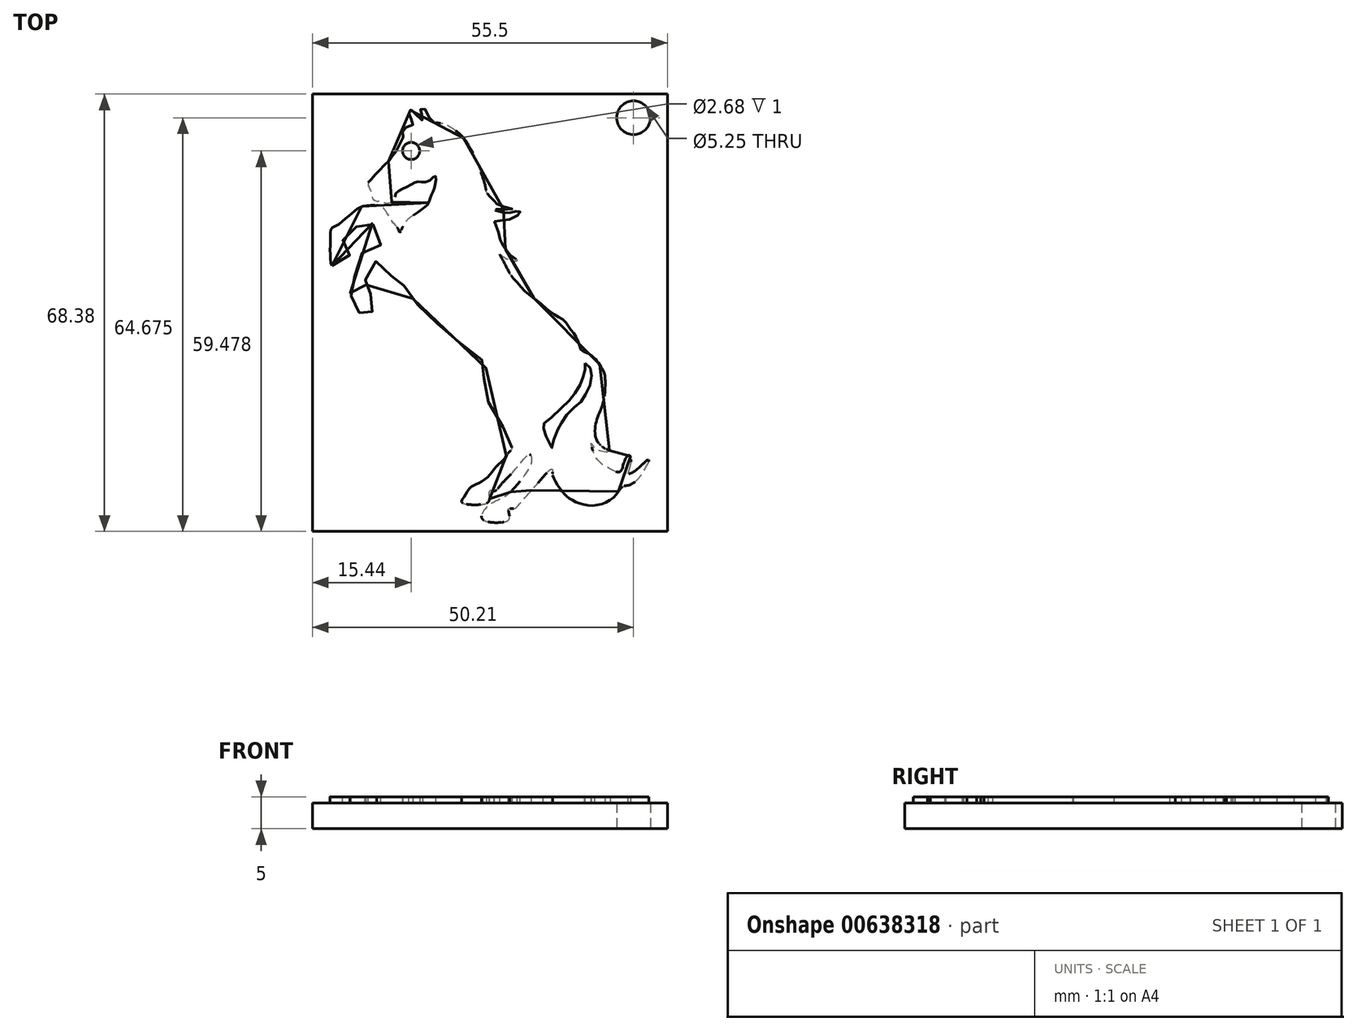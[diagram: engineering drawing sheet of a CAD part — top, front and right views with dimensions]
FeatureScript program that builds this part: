
annotation { "Feature Type Name" : "Feature", "Feature Type Description" : "" }
export const myFeature = defineFeature(function(context is Context, id is Id, definition is map)
    precondition{}
    {
        {
            var Q0;
            Q0=qCreatedBy(makeId("Top.planeOp"),FACE);
            var sketch = newSketch(context, id + "F0", { "sketchPlane" : qUnion([Q0])});
            skFitSpline(sketch, "E0", {"points": [v(-65.46, 22.42) * mm, v(-64.16, 22.86) * mm, v(-63.1, 23.72) * mm, v(-62.52, 24.42) * mm, v(-62.76, 25.41) * mm, v(-63.5, 26.06) * mm, v(-63.75, 26.7) * mm, v(-63.2, 27) * mm, v(-62.44, 27.85) * mm, v(-60.34, 29.37) * mm, v(-59.9, 29.52) * mm, v(-59.26, 29.18) * mm, v(-58.78, 28.21) * mm, v(-58.22, 26.6) * mm, v(-57.88, 25.58) * mm, v(-59.04, 25.63) * mm, v(-60.51, 24.74) * mm, v(-61.14, 23.68) * mm, v(-61.62, 22.08) * mm, v(-62.13, 19.91) * mm, v(-62.61, 19.04) * mm, v(-62.47, 17.81) * mm, v(-61.86, 16.53) * mm, v(-61.72, 15.71) * mm, v(-61.02, 14.9) * mm, v(-60.32, 13.66) * mm, v(-59.45, 14.82) * mm, v(-58.49, 16.7) * mm, v(-59.3, 17.7) * mm, v(-59.38, 17.96) * mm, v(-60.27, 18.27) * mm, v(-60.1, 19) * mm, v(-60.2, 20.25) * mm, v(-59.38, 22.32) * mm, v(-59, 23.1) * mm, v(-57.79, 22.78) * mm, v(-56.8, 21.7) * mm, v(-56.15, 20.78) * mm, v(-55.9, 20.59) * mm, v(-55.69, 20.54) * mm, v(-54.77, 19.6) * mm, v(-53.8, 19.12) * mm, v(-53.06, 17.7) * mm, v(-51.73, 16) * mm, v(-50.23, 14.58) * mm, v(-48.52, 13.03) * mm, v(-46.83, 11.6) * mm, v(-45.1, 10.05) * mm, v(-42.87, 8.36) * mm, v(-41.37, 7.35) * mm, v(-41.26, 7.33) * mm, v(-41.53, 5.64) * mm, v(-41.83, 3.73) * mm, v(-41.49, 2.1) * mm, v(-40.4, 0.06) * mm, v(-39.21, -1.97) * mm, v(-37.83, -4.24) * mm, v(-37.47, -5.26) * mm, v(-37.37, -6.23) * mm, v(-37.97, -6.94) * mm, v(-38.44, -7.7) * mm, v(-39.63, -8.83) * mm, v(-40.83, -10.33) * mm, v(-42.47, -11.56) * mm, v(-43.73, -12.17) * mm, v(-44.75, -13.67) * mm, v(-45.16, -14.56) * mm, v(-42.13, -14.9) * mm, v(-40.86, -14.25) * mm, v(-40.83, -12.92) * mm, v(-40.49, -12.65) * mm, v(-39.98, -12.78) * mm, v(-39.05, -11.83) * mm, v(-37, -9.65) * mm, v(-34.49, -7.11) * mm, v(-34.28, -8.31) * mm, v(-34.82, -9.54) * mm, v(-38.13, -13.47) * mm, v(-40.83, -14.93) * mm, v(-41.99, -17.08) * mm, v(-38.71, -17.66) * mm, v(-37.69, -16.95) * mm, v(-37.83, -15.58) * mm, v(-37.04, -15.55) * mm, v(-35.98, -14.66) * mm, v(-33.42, -11.76) * mm, v(-31.14, -9.37) * mm, v(-30.97, -9.61) * mm, v(-30.93, -10.36) * mm, v(-29.57, -12.72) * mm, v(-28, -14.15) * mm, v(-24.9, -15.07) * mm, v(-21.41, -13.77) * mm, v(-19.98, -12.07) * mm, v(-19.23, -11.93) * mm, v(-18.13, -11.39) * mm, v(-16.77, -9.78) * mm, v(-15.9, -7.87) * mm, v(-16.57, -8.31) * mm, v(-18.03, -9.61) * mm, v(-19.1, -10.09) * mm, v(-18.82, -8.93) * mm, v(-18.85, -7.26) * mm, v(-19.3, -7.36) * mm, v(-19.94, -8.83) * mm, v(-20.46, -9.78) * mm, v(-22.16, -9.24) * mm, v(-24.28, -7.36) * mm, v(-24.93, -5.31) * mm, v(-24.52, -5.93) * mm, v(-23.63, -6.47) * mm, v(-21.85, -6.64) * mm, v(-23.02, -6) * mm, v(-23.77, -5.28) * mm, v(-24.13, -4.7) * mm, v(-24.28, -2.6) * mm, v(-23.55, -0.37) * mm, v(-23.12, 0.89) * mm, v(-22.82, 2.35) * mm, v(-22.77, 4.93) * mm, v(-23.13, 6.21) * mm, v(-24.97, 8.44) * mm, v(-26.43, 9.2) * mm, v(-26.74, 9.97) * mm, v(-27.4, 11.52) * mm, v(-28.21, 12.57) * mm, v(-29.06, 13.78) * mm, v(-30.44, 14.69) * mm, v(-31.86, 15.7) * mm, v(-33.75, 17.26) * mm, v(-35.08, 18.3) * mm, v(-36.72, 20.05) * mm, v(-37.6, 21.13) * mm, v(-38.5, 22.88) * mm, v(-39.2, 24.2) * mm, v(-38.18, 23.55) * mm, v(-36.49, 23.27) * mm, v(-37.48, 24) * mm, v(-38.18, 24.85) * mm, v(-39.1, 26.39) * mm, v(-39.62, 28.37) * mm, v(-40.01, 29.33) * mm, v(-38.12, 29.58) * mm, v(-36.03, 30.74) * mm, v(-36.09, 30.9) * mm, v(-37.19, 30.82) * mm, v(-38.26, 30.68) * mm, v(-40.1, 31.22) * mm, v(-37.25, 31.25) * mm, v(-39.34, 31.9) * mm, v(-40.01, 32.46) * mm, v(-40.72, 33.2) * mm, v(-41.23, 33.85) * mm, v(-41.51, 35.03) * mm, v(-42.41, 37.77) * mm, v(-43.18, 39.6) * mm, v(-44.73, 42.24) * mm, v(-45.77, 43.27) * mm, v(-47.97, 44.6) * mm, v(-49.53, 44.88) * mm, v(-50.35, 45.75) * mm, v(-51.16, 47.15) * mm, v(-51.65, 46.8) * mm, v(-51.5, 46.23) * mm, v(-51.28, 45.19) * mm, v(-52.52, 46.29) * mm, v(-53.03, 46.8) * mm, v(-53.34, 46.69) * mm, v(-53.4, 46.23) * mm, v(-53.03, 45.3) * mm, v(-52.77, 44.48) * mm, v(-53.76, 44.11) * mm, v(-54.33, 43.58) * mm, v(-54.33, 42.84) * mm, v(-54.41, 42.08) * mm, v(-54.95, 41.49) * mm, v(-55.03, 41.15) * mm, v(-55.2, 40.56) * mm, v(-55.8, 39.93) * mm, v(-56.2, 39.34) * mm, v(-56.79, 38.55) * mm, v(-57.66, 37.84) * mm, v(-58.17, 37.17) * mm, v(-58.8, 36.6) * mm, v(-59.44, 35.81) * mm, v(-59.72, 35.58) * mm, v(-59.8, 35.1) * mm, v(-59.58, 34.51) * mm, v(-59.3, 33.78) * mm, v(-58.99, 32.79) * mm, v(-58.17, 32.56) * mm, v(-58.06, 32.62) * mm, v(-57.15, 32.28) * mm, v(-55.85, 32.6) * mm, v(-55.46, 33.7) * mm, v(-54.44, 34.43) * mm, v(-52.6, 35.36) * mm, v(-51.76, 35.56) * mm, v(-50.37, 35.61) * mm, v(-49.3, 36.43) * mm, v(-49.27, 35.3) * mm, v(-49.61, 34.06) * mm, v(-50.06, 33.07) * mm, v(-50.57, 31.94) * mm, v(-52.8, 30.27) * mm, v(-54.24, 28.83) * mm, v(-54.84, 27.65) * mm, v(-55.12, 28.2) * mm, v(-56.05, 29.42) * mm, v(-57.73, 31.74) * mm, v(-59.01, 31.9) * mm, v(-60.19, 31.84) * mm, v(-60.8, 31.68) * mm, v(-61.65, 31.22) * mm, v(-62.27, 30.64) * mm, v(-63.24, 29.9) * mm, v(-64.3, 28.96) * mm, v(-65.16, 28.52) * mm, v(-65.6, 28.1) * mm, v(-65.68, 27.36) * mm, v(-65.7, 26.04) * mm, v(-65.74, 24.63) * mm, v(-65.66, 23.3) * mm, v(-65.46, 22.42) * mm]});
            skFitSpline(sketch, "E1", {"points": [v(-25.87, 7.2) * mm, v(-25.87, 6.5) * mm, v(-26.13, 5.37) * mm, v(-26.47, 4.27) * mm, v(-27.29, 2.74) * mm, v(-28.3, 1.39) * mm, v(-30.17, -0.36) * mm, v(-32.14, -2.17) * mm, v(-32.43, -2.31) * mm, v(-32.28, -3.27) * mm, v(-31.89, -4.4) * mm, v(-31.35, -5.53) * mm, v(-31.1, -5.9) * mm, v(-31.04, -6.04) * mm, v(-30.56, -3.98) * mm, v(-29.91, -2.76) * mm, v(-29.32, -1.7) * mm, v(-28, -0.05) * mm, v(-26.72, 0.96) * mm, v(-25.96, 2.1) * mm, v(-25.14, 3.7) * mm, v(-24.88, 5.51) * mm, v(-25.17, 6.56) * mm, v(-25.87, 7.2) * mm]});
            skCircle(sketch, "E2", {"center": v(-53.07, 40.38) * mm, "radius": 1.34 * mm});
            skSolve(sketch);
        }
        {
            var Q0;
            Q0=makeQuery(id+"F0.imprint","IMPRINT",FACE,{"disambiguationData":[TD([[makeQuery(id+"F0.imprint","IMPRINT",EDGE,{"derivedFrom":sQuery(id+"F0.wireOp",EDGE,"E0")}),1.0]])]});
            extrude(context, id + "F1", {"entities" : qUnion([Q0]), "depth" : 5 * mm, "offsetDistance" : 25 * mm});
        }
        {
            var Q0;
            Q0=qCreatedBy(makeId("Top.planeOp"),FACE);
            var sketch = newSketch(context, id + "F2", { "sketchPlane" : qUnion([Q0])});
            skLineSegment(sketch, "E3.bottom", {"start": v(-68.5, 49.28) * mm, "end": v(-13, 49.28) * mm});
            skLineSegment(sketch, "E3.top", {"start": v(-68.5, -19.1) * mm, "end": v(-13, -19.1) * mm});
            skLineSegment(sketch, "E3.left", {"start": v(-68.5, 49.28) * mm, "end": v(-68.5, -19.1) * mm});
            skLineSegment(sketch, "E3.right", {"start": v(-13, 49.28) * mm, "end": v(-13, -19.1) * mm});
            skCircle(sketch, "E4", {"center": v(-18.3, 45.57) * mm, "radius": 2.63 * mm});
            skSolve(sketch);
        }
        {
            var Q0;
            Q0 = qSketchRegion(id + "F2", true);
            extrude(context, id + "F3", {"entities" : qUnion([Q0]), "operationType" : NewBodyOperationType.ADD, "depth" : 4 * mm, "offsetDistance" : 25 * mm});
        }
    });
